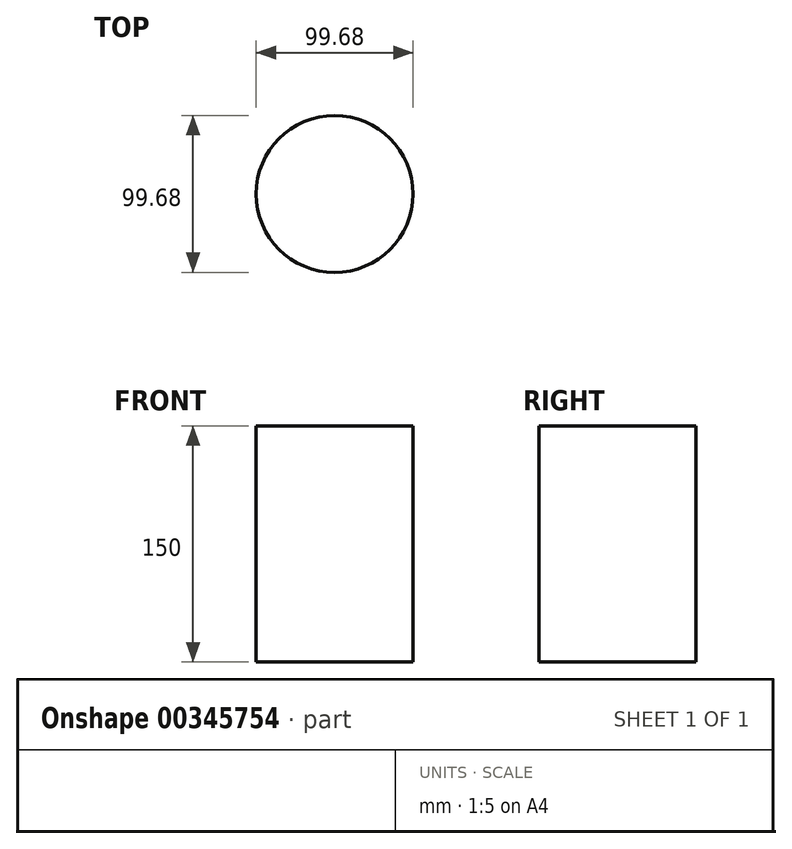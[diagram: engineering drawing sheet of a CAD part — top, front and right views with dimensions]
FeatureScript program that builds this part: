
annotation { "Feature Type Name" : "Feature", "Feature Type Description" : "" }
export const myFeature = defineFeature(function(context is Context, id is Id, definition is map)
    precondition{}
    {
        {
            var Q0;
            Q0=qCreatedBy(makeId("Top.planeOp"),FACE);
            var sketch = newSketch(context, id + "F0", { "sketchPlane" : qUnion([Q0])});
            skCircle(sketch, "E0", {"center": v(0, 0) * mm, "radius": 49.84 * mm});
            skSolve(sketch);
        }
        {
            var Q0;
            Q0=makeQuery(id+"F0.imprint","IMPRINT",FACE,{"disambiguationData":[TD([[makeQuery(id+"F0.imprint","IMPRINT",EDGE,{"derivedFrom":sQuery(id+"F0.wireOp",EDGE,"E0")}),1.0]])]});
            extrude(context, id + "F1", {"entities" : qUnion([Q0]), "depth" : 150 * mm});
        }
    });
